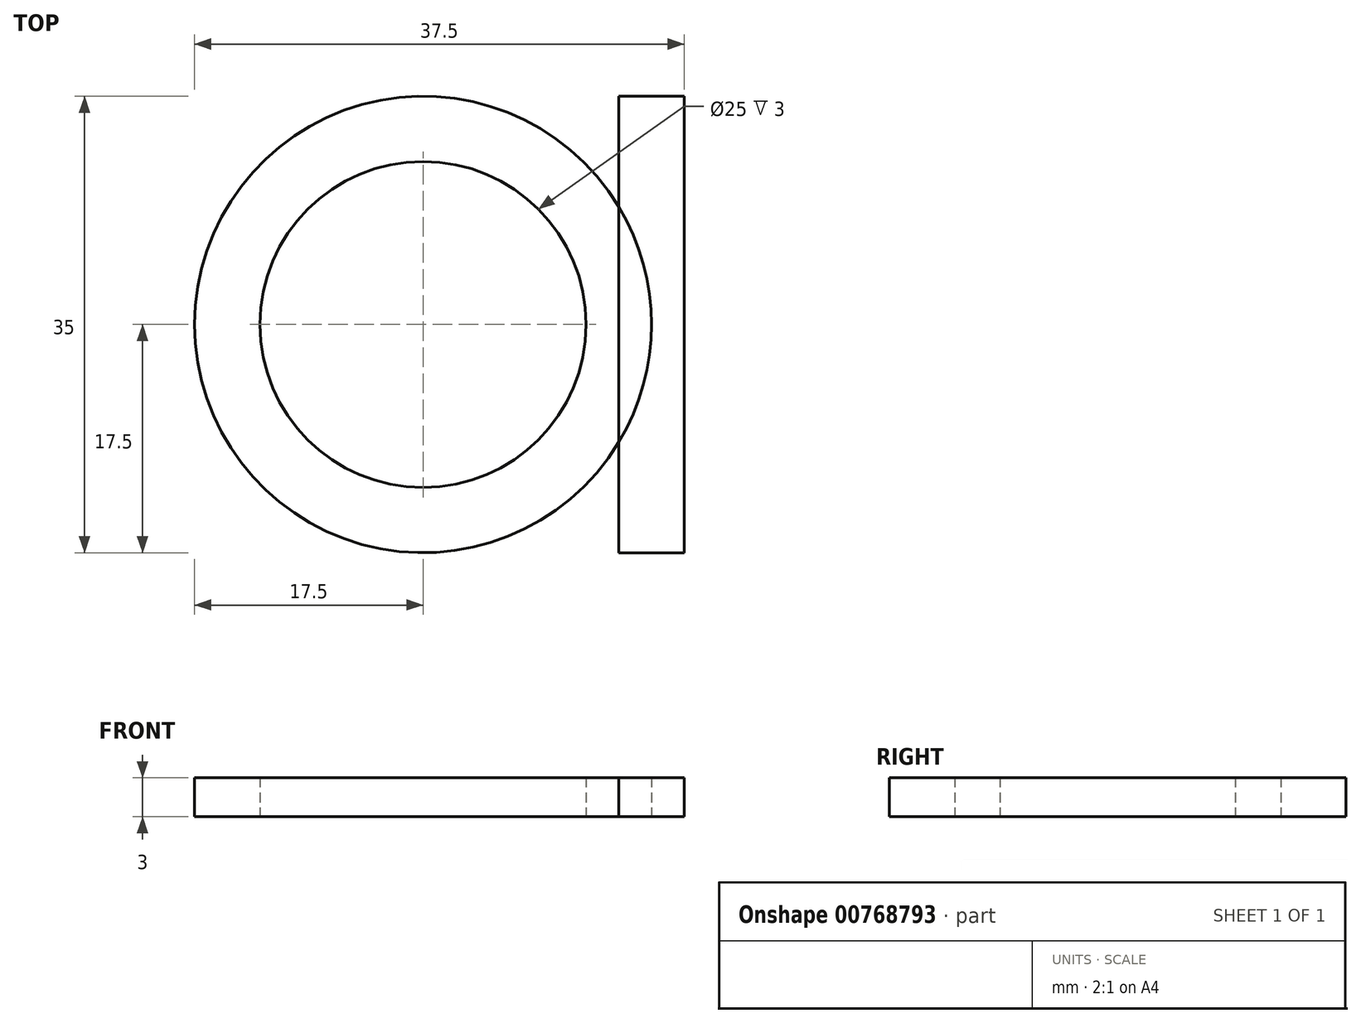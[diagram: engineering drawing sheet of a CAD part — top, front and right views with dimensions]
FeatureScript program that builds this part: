
annotation { "Feature Type Name" : "Feature", "Feature Type Description" : "" }
export const myFeature = defineFeature(function(context is Context, id is Id, definition is map)
    precondition{}
    {
        {
            var Q0;
            Q0=qCreatedBy(makeId("Top.planeOp"),FACE);
            var sketch = newSketch(context, id + "F0", { "sketchPlane" : qUnion([Q0])});
            skCircle(sketch, "E0", {"center": v(0, 0) * mm, "radius": 17.5 * mm});
            skCircle(sketch, "E1", {"center": v(0, 0) * mm, "radius": 12.5 * mm});
            skLineSegment(sketch, "E2.bottom", {"start": v(15, 17.5) * mm, "end": v(20, 17.5) * mm});
            skLineSegment(sketch, "E2.top", {"start": v(15, -17.5) * mm, "end": v(20, -17.5) * mm});
            skLineSegment(sketch, "E2.left", {"start": v(15, 17.5) * mm, "end": v(15, -17.5) * mm});
            skLineSegment(sketch, "E2.right", {"start": v(20, 17.5) * mm, "end": v(20, -17.5) * mm});
            skSolve(sketch);
        }
        {
            var Q0;
            Q0=makeQuery(id+"F0.imprint","IMPRINT",FACE,{"disambiguationData":[TD([[makeQuery(id+"F0.imprint","IMPRINT",EDGE,{"derivedFrom":sQuery(id+"F0.wireOp",EDGE,"E1")}),-1.0]])]});
            var Q1;
            {var subQ0=sQuery(id+"F0.wireOp",EDGE,"E2.left");var subQ1=sQuery(id+"F0.wireOp",EDGE,"E0");var subQ2=makeQuery(id+"F0.imprint","INTERSECT",VERTEX,{"disambiguationData":[OD(0.0)],"derivedFrom":[subQ1,subQ0]});Q1=makeQuery(id+"F0.imprint","IMPRINT",FACE,{"disambiguationData":[TD([[makeQuery(id+"F0.imprint","IMPRINT",EDGE,{"disambiguationData":[TD([[subQ2,1.0]])],"derivedFrom":subQ1}),1.0]])]});}
            var Q2;
            {var subQ1=sQuery(id+"F0.wireOp",EDGE,"E2.bottom");Q2=makeQuery(id+"F0.imprint","IMPRINT",FACE,{"disambiguationData":[TD([[makeQuery(id+"F0.imprint","IMPRINT",EDGE,{"derivedFrom":subQ1}),-1.0]])]});}
            extrude(context, id + "F1", {"entities" : qUnion([Q0, Q1, Q2]), "depth" : 3 * mm, "offsetDistance" : 25 * mm});
        }
    });
